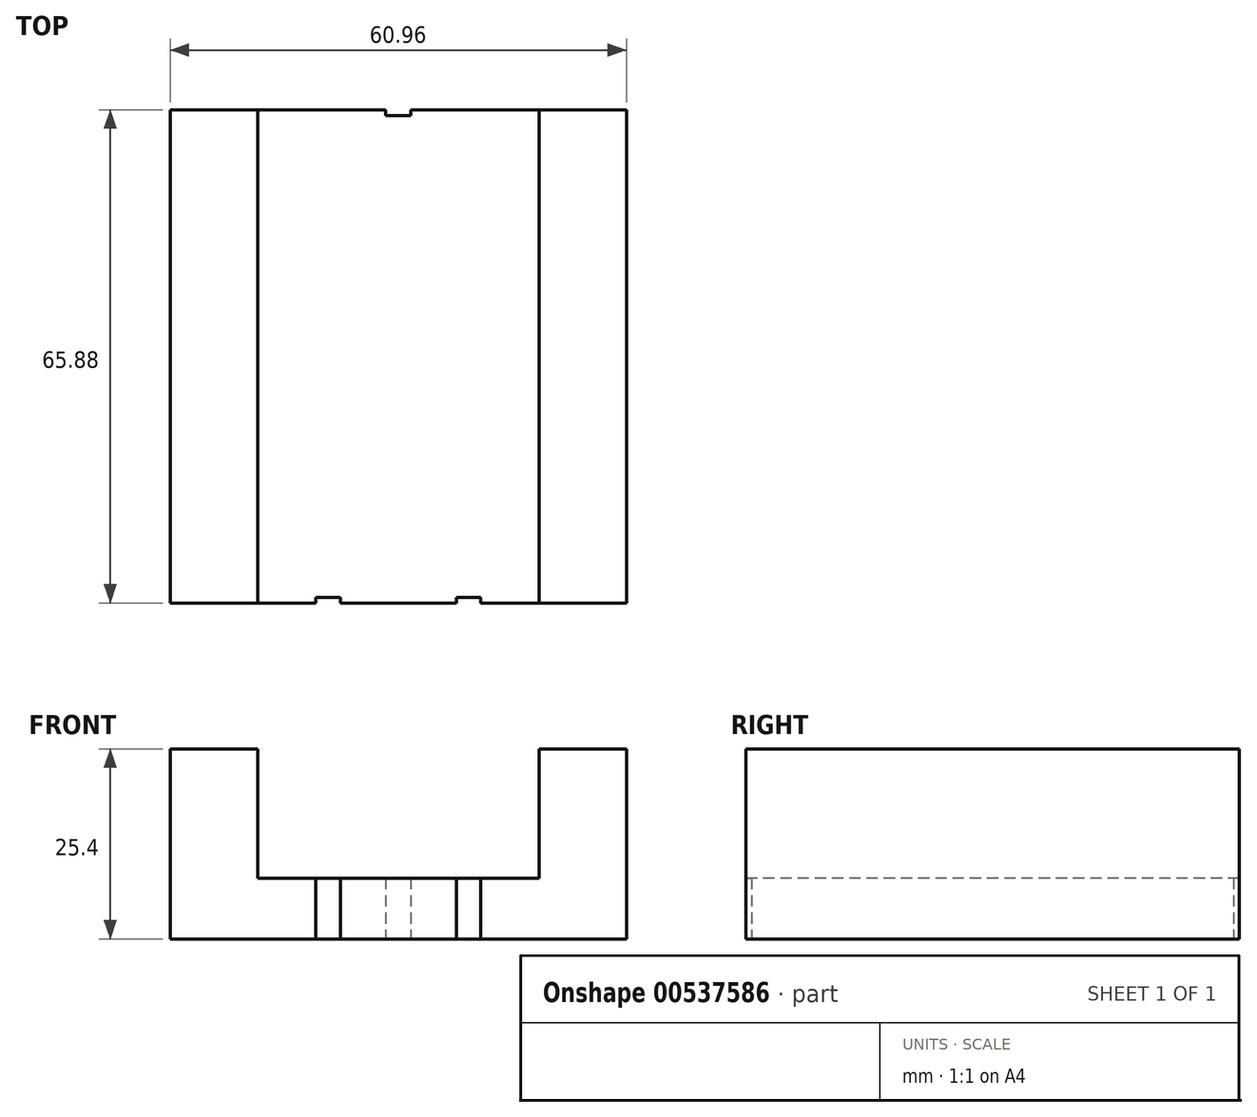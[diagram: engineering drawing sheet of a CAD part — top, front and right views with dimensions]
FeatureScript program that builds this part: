
annotation { "Feature Type Name" : "Feature", "Feature Type Description" : "" }
export const myFeature = defineFeature(function(context is Context, id is Id, definition is map)
    precondition{}
    {
        {
            var Q0;
            Q0=qCreatedBy(makeId("Top.planeOp"),FACE);
            var sketch = newSketch(context, id + "F0", { "sketchPlane" : qUnion([Q0])});
            skLineSegment(sketch, "E0.bottom", {"start": v(30.48, 32.94) * mm, "end": v(1.65, 32.94) * mm});
            skLineSegment(sketch, "E0.top", {"start": v(30.48, -32.94) * mm, "end": v(11.05, -32.94) * mm});
            skLineSegment(sketch, "E0.left", {"start": v(30.48, 32.94) * mm, "end": v(30.48, -32.94) * mm});
            skLineSegment(sketch, "E0.right", {"start": v(-30.48, 32.94) * mm, "end": v(-30.48, -32.94) * mm});
            skPoint(sketch, "E0.middle", {"position": v(0, 0) * mm});
            skLineSegment(sketch, "E1", {"start": v(-18.8, 32.94) * mm, "end": v(-18.8, -32.94) * mm});
            skLineSegment(sketch, "E2", {"start": v(18.8, 32.94) * mm, "end": v(18.8, -32.94) * mm});
            skLineSegment(sketch, "E3.top", {"start": v(-1.65, 32.18) * mm, "end": v(1.65, 32.18) * mm});
            skLineSegment(sketch, "E3.left", {"start": v(-1.65, 32.94) * mm, "end": v(-1.65, 32.18) * mm});
            skLineSegment(sketch, "E3.right", {"start": v(1.65, 32.94) * mm, "end": v(1.65, 32.18) * mm});
            skLineSegment(sketch, "E4.trimOffspring", {"start": v(-1.65, 32.94) * mm, "end": v(-30.48, 32.94) * mm});
            skLineSegment(sketch, "E5", {"start": v(9.4, -32.94) * mm, "end": v(9.4, -12.05) * mm, "construction": true});
            skLineSegment(sketch, "E6.top", {"start": v(7.75, -32.18) * mm, "end": v(11.05, -32.18) * mm});
            skLineSegment(sketch, "E6.left", {"start": v(7.75, -32.94) * mm, "end": v(7.75, -32.18) * mm});
            skLineSegment(sketch, "E6.right", {"start": v(11.05, -32.94) * mm, "end": v(11.05, -32.18) * mm});
            skLineSegment(sketch, "E7.trimOffspring", {"start": v(7.75, -32.94) * mm, "end": v(-7.75, -32.94) * mm});
            skLineSegment(sketch, "E8.MirrorCS", {"start": v(-7.75, -32.18) * mm, "end": v(-11.05, -32.18) * mm});
            skLineSegment(sketch, "E9.MirrorCS", {"start": v(-7.75, -32.94) * mm, "end": v(-7.75, -32.18) * mm});
            skLineSegment(sketch, "E10.MirrorCS", {"start": v(-11.05, -32.94) * mm, "end": v(-11.05, -32.18) * mm});
            skLineSegment(sketch, "E11.trimOffspring", {"start": v(-11.05, -32.94) * mm, "end": v(-30.48, -32.94) * mm});
            skSolve(sketch);
        }
        {
            var Q0;
            {var subQ1=sQuery(id+"F0.wireOp",EDGE,"E1");Q0=makeQuery(id+"F0.imprint","IMPRINT",FACE,{"disambiguationData":[TD([[makeQuery(id+"F0.imprint","IMPRINT",EDGE,{"derivedFrom":subQ1}),1.0]])]});}
            extrude(context, id + "F1", {"entities" : qUnion([Q0]), "depth" : 8.13 * mm, "offsetDistance" : 25.4 * mm});
        }
        {
            var Q0;
            {var subQ0=sQuery(id+"F0.wireOp",EDGE,"E0.right");Q0=makeQuery(id+"F0.imprint","IMPRINT",FACE,{"disambiguationData":[TD([[makeQuery(id+"F0.imprint","IMPRINT",EDGE,{"derivedFrom":subQ0}),1.0]])]});}
            var Q1;
            {var subQ0=sQuery(id+"F0.wireOp",EDGE,"E0.left");Q1=makeQuery(id+"F0.imprint","IMPRINT",FACE,{"disambiguationData":[TD([[makeQuery(id+"F0.imprint","IMPRINT",EDGE,{"derivedFrom":subQ0}),-1.0]])]});}
            extrude(context, id + "F2", {"entities" : qUnion([Q0, Q1]), "operationType" : NewBodyOperationType.ADD, "depth" : 25.4 * mm, "offsetDistance" : 25.4 * mm});
        }
    });
